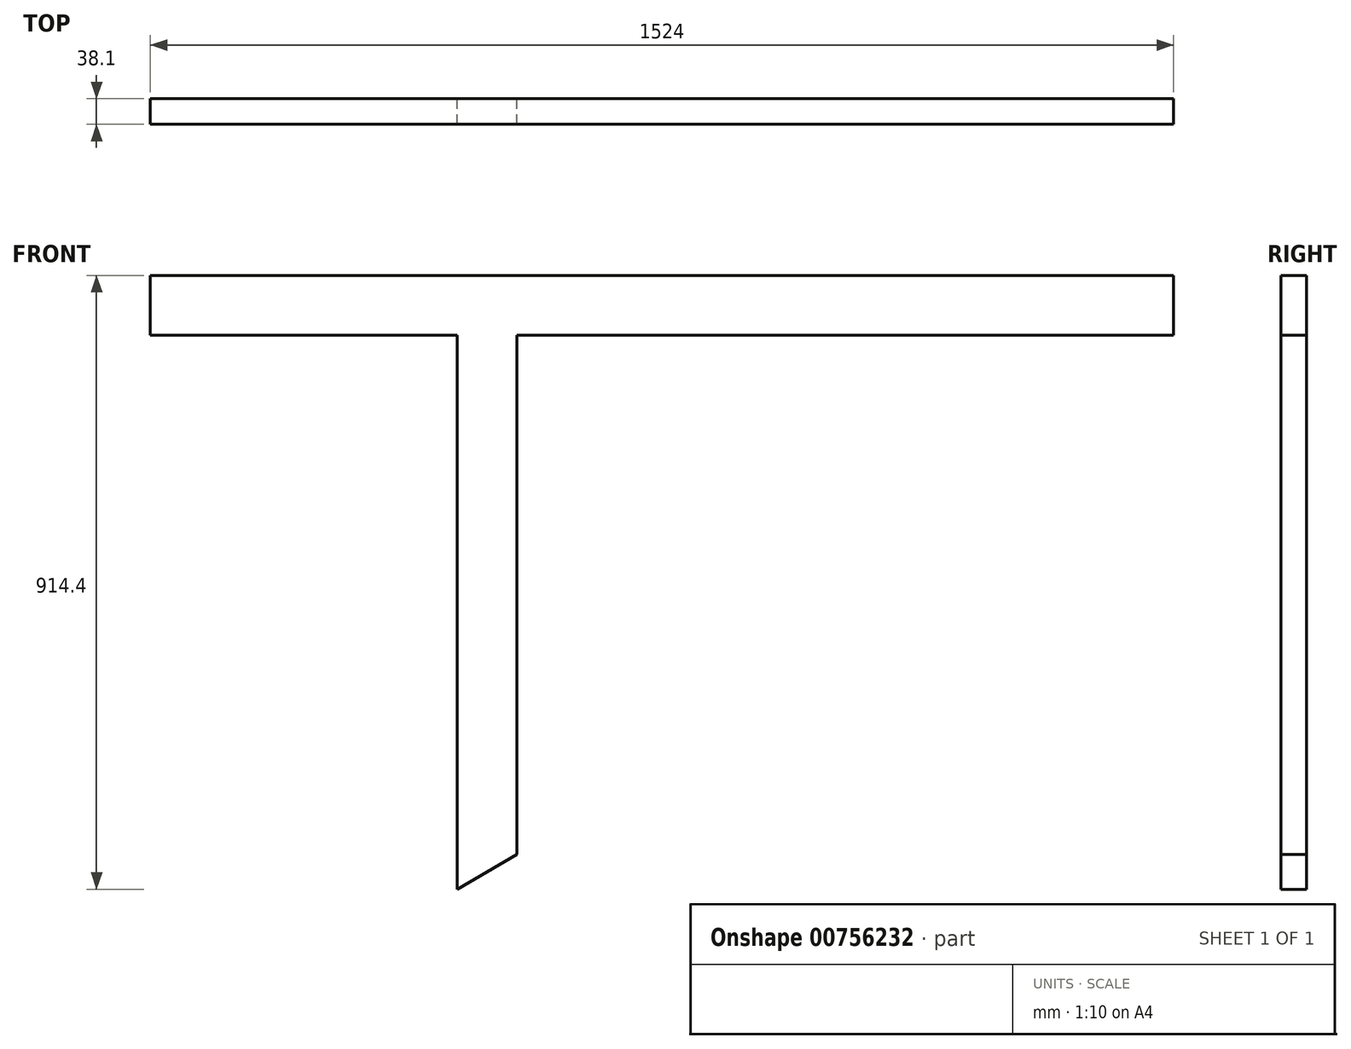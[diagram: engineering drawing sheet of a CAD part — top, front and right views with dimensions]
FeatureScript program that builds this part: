
annotation { "Feature Type Name" : "Feature", "Feature Type Description" : "" }
export const myFeature = defineFeature(function(context is Context, id is Id, definition is map)
    precondition{}
    {
        {
            var Q0;
            Q0=qCreatedBy(makeId("Front.planeOp"),FACE);
            var sketch = newSketch(context, id + "F0", { "sketchPlane" : qUnion([Q0])});
            skLineSegment(sketch, "E0.bottom", {"start": v(-44.45, 457.2) * mm, "end": v(44.45, 457.2) * mm});
            skLineSegment(sketch, "E0.top", {"start": v(-44.45, -457.2) * mm, "end": v(44.45, -457.2) * mm});
            skLineSegment(sketch, "E0.left", {"start": v(-44.45, 457.2) * mm, "end": v(-44.45, -457.2) * mm});
            skLineSegment(sketch, "E0.right", {"start": v(44.45, 457.2) * mm, "end": v(44.45, -457.2) * mm});
            skPoint(sketch, "E0.middle", {"position": v(0, 0) * mm});
            skLineSegment(sketch, "E1.bottom", {"start": v(-501.65, 457.2) * mm, "end": v(1022.35, 457.2) * mm});
            skLineSegment(sketch, "E1.top", {"start": v(-501.65, 368.3) * mm, "end": v(1022.35, 368.3) * mm});
            skLineSegment(sketch, "E1.left", {"start": v(-501.65, 457.2) * mm, "end": v(-501.65, 368.3) * mm});
            skLineSegment(sketch, "E1.right", {"start": v(1022.35, 457.2) * mm, "end": v(1022.35, 368.3) * mm});
            skLineSegment(sketch, "E2", {"start": v(-44.45, -457.2) * mm, "end": v(44.45, -405.42) * mm});
            skSolve(sketch);
        }
        {
            var Q0;
            {var subQ5=sQuery(id+"F0.wireOp",EDGE,"E1.left");Q0=makeQuery(id+"F0.imprint","IMPRINT",FACE,{"disambiguationData":[TD([[makeQuery(id+"F0.imprint","IMPRINT",EDGE,{"derivedFrom":subQ5}),1.0]])]});}
            var Q1;
            {var subQ0=sQuery(id+"F0.wireOp",EDGE,"E1.bottom");var subQ1=sQuery(id+"F0.wireOp",EDGE,"E0.left");var subQ2=makeQuery(id+"F0.imprint","INTERSECT",VERTEX,{"derivedFrom":[subQ1,subQ0]});Q1=makeQuery(id+"F0.imprint","IMPRINT",FACE,{"disambiguationData":[TD([[makeQuery(id+"F0.imprint","IMPRINT",EDGE,{"disambiguationData":[TD([[subQ2,-1.0]])],"derivedFrom":subQ1}),1.0]])]});}
            var Q2;
            {var subQ5=sQuery(id+"F0.wireOp",EDGE,"E1.right");Q2=makeQuery(id+"F0.imprint","IMPRINT",FACE,{"disambiguationData":[TD([[makeQuery(id+"F0.imprint","IMPRINT",EDGE,{"derivedFrom":subQ5}),-1.0]])]});}
            var Q3;
            {var subQ0=sQuery(id+"F0.wireOp",EDGE,"E2");Q3=makeQuery(id+"F0.imprint","IMPRINT",FACE,{"disambiguationData":[TD([[makeQuery(id+"F0.imprint","IMPRINT",EDGE,{"derivedFrom":subQ0}),1.0]])]});}
            extrude(context, id + "F1", {"entities" : qUnion([Q0, Q1, Q2, Q3]), "endBound" : BoundingType.SYMMETRIC, "depth" : 38.1 * mm, "offsetDistance" : 25.4 * mm});
        }
    });
